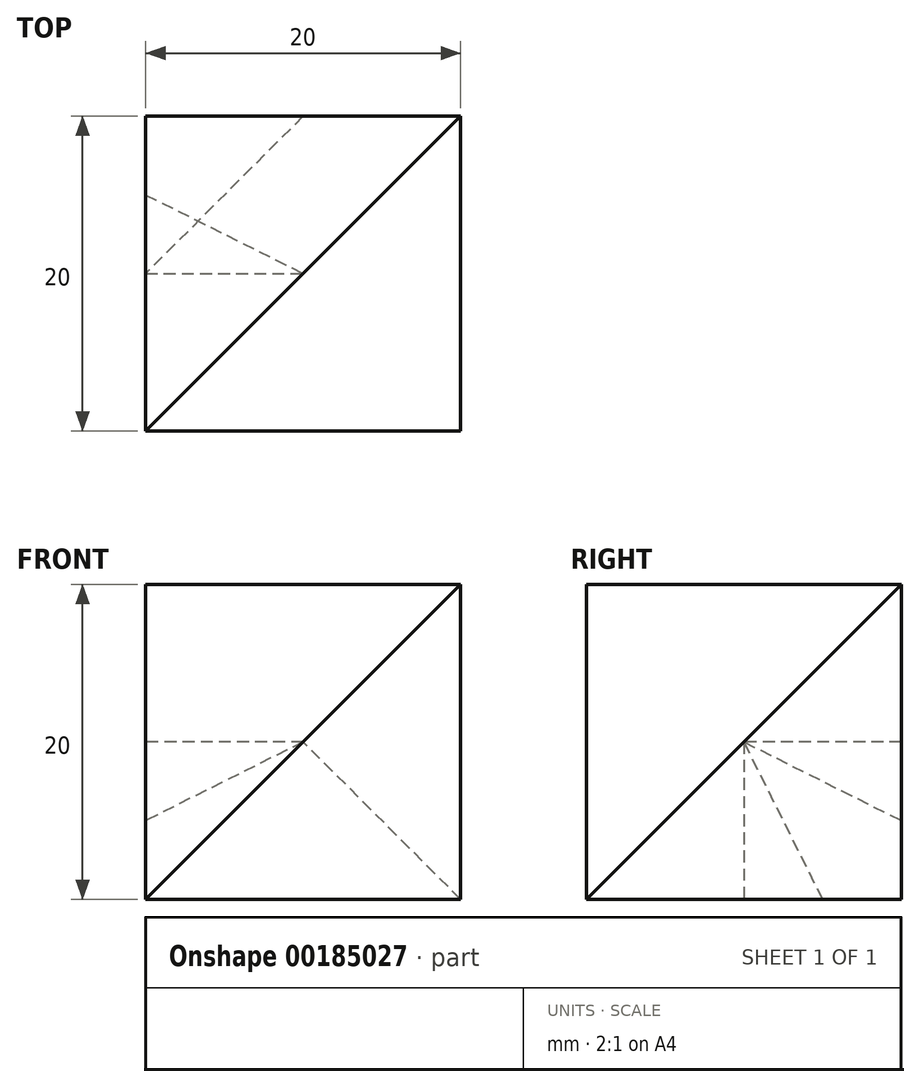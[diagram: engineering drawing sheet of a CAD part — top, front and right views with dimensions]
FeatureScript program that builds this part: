
annotation { "Feature Type Name" : "Feature", "Feature Type Description" : "" }
export const myFeature = defineFeature(function(context is Context, id is Id, definition is map)
    precondition{}
    {
        {
            var Q0;
            Q0=qCreatedBy(makeId("Top.planeOp"),FACE);
            var sketch = newSketch(context, id + "F0", { "sketchPlane" : qUnion([Q0])});
            skLineSegment(sketch, "E0.bottom", {"start": v(10, -10) * mm, "end": v(-10, -10) * mm});
            skLineSegment(sketch, "E0.top", {"start": v(10, 10) * mm, "end": v(-10, 10) * mm});
            skLineSegment(sketch, "E0.left", {"start": v(10, -10) * mm, "end": v(10, 10) * mm});
            skLineSegment(sketch, "E0.right", {"start": v(-10, -10) * mm, "end": v(-10, 10) * mm});
            skPoint(sketch, "E0.middle", {"position": v(0, 0) * mm});
            skSolve(sketch);
        }
        {
            var Q0;
            Q0 = qSketchRegion(id + "F0", true);
            extrude(context, id + "F1", {"entities" : qUnion([Q0]), "depth" : 20 * mm});
        }
        {
            var Q0;
            Q0=makeQuery(id+"F1.opExtrude","CAP_VERTEX",VERTEX,{"disambiguationData":[OSD([sQuery(id+"F0.wireOp",EDGE,"E0.top"),sQuery(id+"F0.wireOp",EDGE,"E0.left")])],"isStart":false});
            var Q1;
            Q1=makeQuery(id+"F1.opExtrude","CAP_VERTEX",VERTEX,{"disambiguationData":[OSD([sQuery(id+"F0.wireOp",EDGE,"E0.bottom"),sQuery(id+"F0.wireOp",EDGE,"E0.right")])],"isStart":true});
            var Q2;
            Q2=makeQuery(id+"F1.opExtrude","CAP_VERTEX",VERTEX,{"disambiguationData":[OSD([sQuery(id+"F0.wireOp",EDGE,"E0.bottom"),sQuery(id+"F0.wireOp",EDGE,"E0.left")])],"isStart":true});
            cPlane(context, id + "F2", {"entities" : qUnion([Q0, Q1, Q2]), "cplaneType" : CPlaneType.THREE_POINT, "offset" : 0 * mm, "width" : 150 * mm, "height" : 150 * mm});
        }
        {
            var Q0;
            Q0=makeQuery(id+"F1.opExtrude","CAP_FACE",FACE,{"disambiguationData":[OSD([sQuery(id+"F0.wireOp",EDGE,"E0.bottom"),sQuery(id+"F0.wireOp",EDGE,"E0.top"),sQuery(id+"F0.wireOp",EDGE,"E0.left"),sQuery(id+"F0.wireOp",EDGE,"E0.right")])],"isStart":false});
            var sketch = newSketch(context, id + "F3", { "sketchPlane" : qUnion([Q0])});
            skLineSegment(sketch, "E1", {"start": v(10, 10) * mm, "end": v(-10, -10) * mm});
            skLineSegment(sketch, "E2", {"start": v(-10, -10) * mm, "end": v(10, -10) * mm});
            skLineSegment(sketch, "E3", {"start": v(10, -10) * mm, "end": v(10, 10) * mm});
            skSolve(sketch);
        }
        {
            var Q0;
            Q0 = qSketchRegion(id + "F3", true);
            var Q1;
            Q1=qCreatedBy(id+"F2.planeOp",FACE);
            extrude(context, id + "F4", {"entities" : qUnion([Q0]), "operationType" : NewBodyOperationType.REMOVE, "endBound" : BoundingType.UP_TO_SURFACE, "oppositeDirection" : true, "endBoundEntityFace" : qUnion([Q1]), "depth" : 25 * mm});
        }
        {
            var Q0;
            Q0=makeQuery(id+"F1.opExtrude","CAP_VERTEX",VERTEX,{"disambiguationData":[OSD([sQuery(id+"F0.wireOp",EDGE,"E0.top"),sQuery(id+"F0.wireOp",EDGE,"E0.right")])],"isStart":false});
            var Q1;
            Q1=makeQuery(id+"F1.opExtrude","CAP_VERTEX",VERTEX,{"disambiguationData":[OSD([sQuery(id+"F0.wireOp",EDGE,"E0.top"),sQuery(id+"F0.wireOp",EDGE,"E0.left")])],"isStart":true});
            var Q2;
            {var subQ0=sQuery(id+"F0.wireOp",EDGE,"E0.right");Q2=makeQuery(id+"F4.boolean.opBoolean","MERGE",VERTEX,{"derivedFrom":[makeQuery(id+"F1.opExtrude","CAP_VERTEX",VERTEX,{"disambiguationData":[OSD([sQuery(id+"F0.wireOp",EDGE,"E0.bottom"),subQ0])],"isStart":true}),makeQuery(id+"F4.opExtrude","CAP_VERTEX",VERTEX,{"disambiguationData":[OSD([sQuery(id+"F0.wireOp",EDGE,"E0.top"),subQ0,dummyQuery(id+"F2.planeOp",FACE),sQuery(id+"F3.wireOp",EDGE,"E1"),sQuery(id+"F3.wireOp",EDGE,"E2"),sQuery(id+"F3.wireOp",EDGE,"E3")])],"isStart":false})]});}
            cPlane(context, id + "F5", {"entities" : qUnion([Q0, Q1, Q2]), "cplaneType" : CPlaneType.THREE_POINT, "offset" : 25 * mm, "width" : 150 * mm, "height" : 150 * mm});
        }
        {
            var Q0;
            Q0=qCreatedBy(id+"F5.planeOp",FACE);
            var sketch = newSketch(context, id + "F6", { "sketchPlane" : qUnion([Q0])});
            skLineSegment(sketch, "E4.0.2", {"start": v(12.25, 21.21) * mm, "end": v(20.41, 7.07) * mm, "construction": true});
            skLineSegment(sketch, "E4.0.3", {"start": v(20.41, 7.07) * mm, "end": v(12.25, -7.07) * mm, "construction": true});
            skLineSegment(sketch, "E5.0.1", {"start": v(-12.25, 7.07) * mm, "end": v(-4.08, 21.21) * mm, "construction": true});
            skLineSegment(sketch, "E5.0.2", {"start": v(-4.08, 21.21) * mm, "end": v(12.25, 21.21) * mm, "construction": true});
            skLineSegment(sketch, "E6.0.0", {"start": v(-4.08, -7.07) * mm, "end": v(-12.25, 7.07) * mm, "construction": true});
            skLineSegment(sketch, "E6.0.3", {"start": v(12.25, -7.07) * mm, "end": v(-4.08, -7.07) * mm, "construction": true});
            skLineSegment(sketch, "E7", {"start": v(12.25, 21.21) * mm, "end": v(12.25, -7.07) * mm});
            skLineSegment(sketch, "E8", {"start": v(-12.25, 7.07) * mm, "end": v(12.25, -7.07) * mm});
            skLineSegment(sketch, "E9", {"start": v(12.25, 21.21) * mm, "end": v(-12.25, 7.07) * mm});
            skSolve(sketch);
        }
        {
            var Q0;
            Q0 = qSketchRegion(id + "F6", true);
            extrude(context, id + "F7", {"entities" : qUnion([Q0]), "operationType" : NewBodyOperationType.REMOVE, "oppositeDirection" : true, "depth" : 25 * mm});
        }
    });
